# Revit family: Plumbing_Drainage_ABN_INSTAL_CT-FASER_Metal-casing_Pipe-Accessories_Ball-valve
name_source: partatom
category: Pipe Accessories
revit_build: Autodesk Revit 2015 (Build: 20140606_1530(x64)
units: mm (PartAtom-declared; Revit-internal decimal feet)

## types (7) — shared parameters
Autor = A3D Consulting
Autor.URL = www.a3d.es
BIMobject category = Valves
Brand url = http://abnpipesystems.com
Design country = Spain
Edition number = 1
IFC Classification = Pipe Fitting
Installation instructions = http://www.abnpipesystems.com
Manufacturer = ABN Pipe Systems
Manufacturer country = Spain
Manufacturer name = ABN Pipe Systems
Material main = Polypropylene
Modelado por = 006
Modificado por = 000
NBS Reference Code = 62-64
NBS Reference Description = Pipe Fittings
Product Guid = 88f48b91-137d-4912-8428-deabc79b4f07
Product SKU = instal_metal-casing_ball-valve
Product data url = https://bimobject.com
Product family = Plumbing
Product group = Valves
Product url = http://www.abnpipesystems.com
QR code = http://bimobject.com
Revisado por = 004
Technical description = http://www.abnpipesystems.com
UNSPSC Code = 401416
URL = http://www.abnpipesystems.com
Uniclass 1.4 Code = L73121
Uniclass 1.4 Description = Pipes and fittings
Uniclass 2.0 Code = PR-62-64
Uniclass 2.0 Description = Pipe Fittings
Versión = L2.01
Youtube clip = https://www.youtube.com
zero-valued in all types: Nominal height, Nominal width, Weight Net (Kg)

## per-type parameters (varying)
| type | Conexión.Longitud | Cuello.Altura | Cuello.Longitud | Cuello.Radio | Cuerpo.Anchura | Cuerpo.Central.Longitud | Cuerpo.Radio.Exterior | Cuerpo.Radio.Interior | DN | Maneta.Tipo | Referencia |
| DN 25 | 12 mm  [stored 0.0393701 ft] | 13 mm | 5 mm  [stored 0.0164042 ft] | 15 mm  [stored 0.0492126 ft] | 36 mm  [stored 0.11811 ft] | 47 mm  [stored 0.154199 ft] | 44 mm  [stored 0.144357 ft] | 12 mm  [stored 0.0393701 ft] | 25 mm | ABN_INSTAL_Componente_Maneta_DN20-25 : Estándar | D3VE025000000 |
| DN 20 | 10 mm  [stored 0.0328084 ft] | 15 mm  [stored 0.0492126 ft] | 4 mm  [stored 0.0131234 ft] | 15 mm  [stored 0.0492126 ft] | 30 mm  [stored 0.0984252 ft] | 44 mm  [stored 0.144357 ft] | 41 mm  [stored 0.134514 ft] | 10 mm  [stored 0.0328084 ft] | 20 mm | ABN_INSTAL_Componente_Maneta_DN20-25 : Estándar | D3VE020000000 |
| DN 32 | 14 mm  [stored 0.0459318 ft] | 4 mm  [stored 0.0131234 ft] | 6 mm  [stored 0.019685 ft] | 18 mm  [stored 0.0590551 ft] | 47 mm  [stored 0.154199 ft] | 48 mm  [stored 0.15748 ft] | 48 mm  [stored 0.15748 ft] | 16 mm  [stored 0.0524934 ft] | 32 mm | ABN_INSTAL_Componente_Maneta_DN32 : Estándar | D3VE032000000 |
| DN 40 | 14 mm  [stored 0.0459318 ft] | 8 mm  [stored 0.0262467 ft] | 8 mm  [stored 0.0262467 ft] | 23 mm  [stored 0.0754593 ft] | 60 mm  [stored 0.19685 ft] | 69 mm  [stored 0.226378 ft] | 65 mm  [stored 0.213255 ft] | 20 mm  [stored 0.0656168 ft] | 40 mm | ABN_INSTAL_Componente_Maneta_DN40-50 : Estándar | D3VE040000000 |
| DN 50 | 17 mm | 4 mm  [stored 0.0131234 ft] | 7 mm  [stored 0.0229659 ft] | 23 mm  [stored 0.0754593 ft] | 69 mm  [stored 0.226378 ft] | 72 mm  [stored 0.23622 ft] | 117 mm  [stored 0.383858 ft] | 25 mm  [stored 0.082021 ft] | 50 mm | ABN_INSTAL_Componente_Maneta_DN40-50 : Estándar | D3VE050000000 |
| DN 63 | 20 mm  [stored 0.0656168 ft] | 13 mm | 9 mm  [stored 0.0295276 ft] | 13 mm | 83 mm  [stored 0.27231 ft] | 79 mm | 140 mm  [stored 0.459318 ft] | 32 mm  [stored 0.104987 ft] | 63 mm | ABN_INSTAL_Componente_Maneta_DN63-75 : Estándar | D3VE063000000 |
| DN 75 | 18 mm  [stored 0.0590551 ft] | 7 mm  [stored 0.0229659 ft] | 8 mm  [stored 0.0262467 ft] | 13 mm | 98 mm  [stored 0.321522 ft] | 107 mm  [stored 0.35105 ft] | 227 mm  [stored 0.744751 ft] | 37 mm  [stored 0.121391 ft] | 75 mm | ABN_INSTAL_Componente_Maneta_DN63-75 : Estándar | D3VE075000000 |

note: [stored X ft] marks values corroborated as IEEE doubles in the binary element streams (Revit-internal decimal feet)
